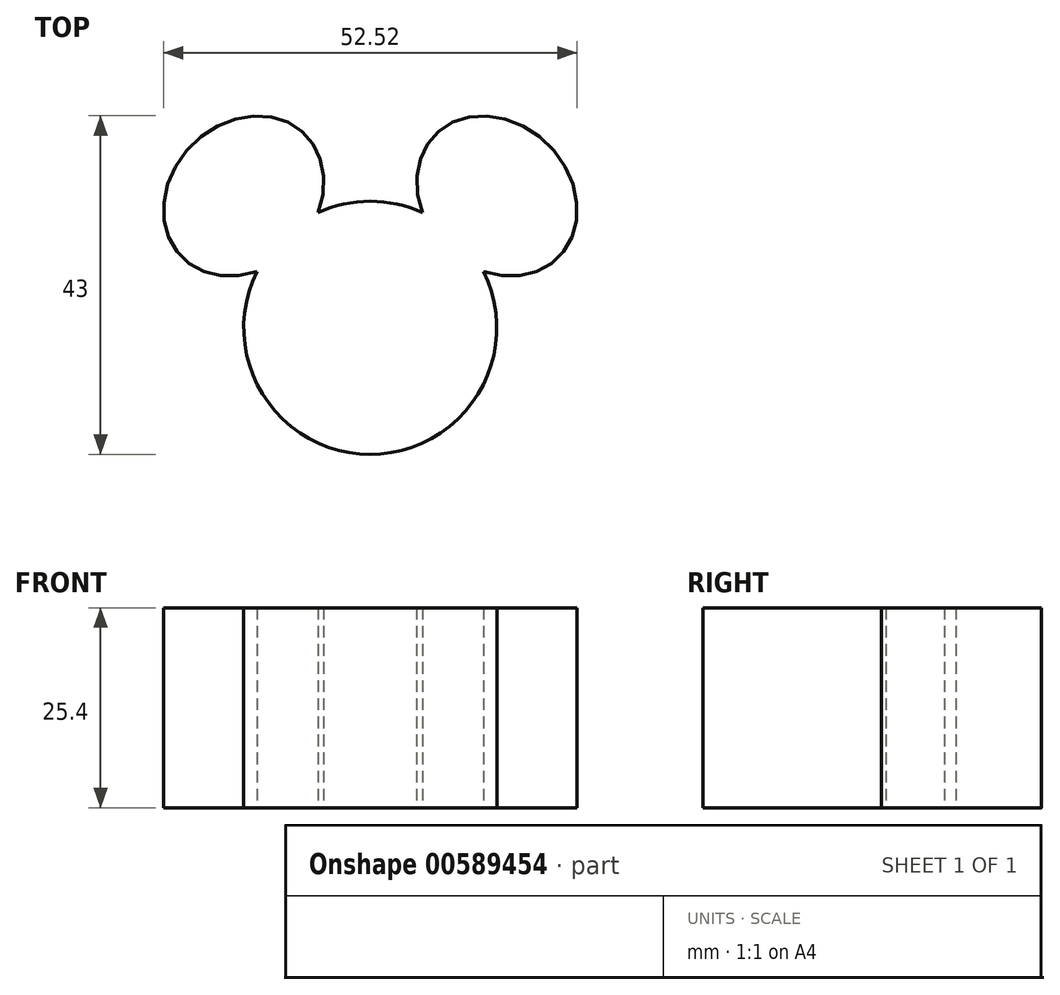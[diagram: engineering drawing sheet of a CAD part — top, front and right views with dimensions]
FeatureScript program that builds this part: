
annotation { "Feature Type Name" : "Feature", "Feature Type Description" : "" }
export const myFeature = defineFeature(function(context is Context, id is Id, definition is map)
    precondition{}
    {
        {
            var Q0;
            Q0=qCreatedBy(makeId("Top.planeOp"),FACE);
            var sketch = newSketch(context, id + "F0", { "sketchPlane" : qUnion([Q0])});
            skCircle(sketch, "E0", {"center": v(0, 17.14) * mm, "radius": 16.07 * mm});
            skEllipse(sketch, "E1", {"center": v(16.08, 33.89) * mm, "majorRadius": 9.24 * mm, "minorRadius": 11.04 * mm, "majorAxis": v(0.7, 0.7)});
            skPoint(sketch, "E1.centerSnap0", {"position": v(-7.3, 33.89) * mm});
            skEllipse(sketch, "E2.MirrorC", {"center": v(-16.08, 33.89) * mm, "majorRadius": 9.24 * mm, "minorRadius": 11.04 * mm, "majorAxis": v(-0.7, 0.7)});
            skSolve(sketch);
        }
        {
            var Q0;
            Q0 = qSketchRegion(id + "F0", true);
            extrude(context, id + "F1", {"entities" : qUnion([Q0]), "depth" : 25.4 * mm, "offsetDistance" : 25.4 * mm});
        }
    });
